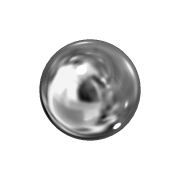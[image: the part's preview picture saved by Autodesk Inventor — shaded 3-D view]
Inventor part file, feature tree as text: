
AUTODESK INVENTOR PART (.ipt)
format: ipt  version: 2019 (Build 230136000, 136)  size: 105,984 bytes
history: native  units: mm
features: revolve x1, sketch x1
ambient origin geometry x8: Origin, YZ Plane, XZ Plane, XY Plane, X Axis, Y Axis, Z Axis, Center Point
bodies: Volumenkörper1 (feature_tree)
feature tree (2):
  revolve  "Umdrehung1"
  sketch  "Skizze1"  dims[d0=2.45mm d1=90.0deg]
